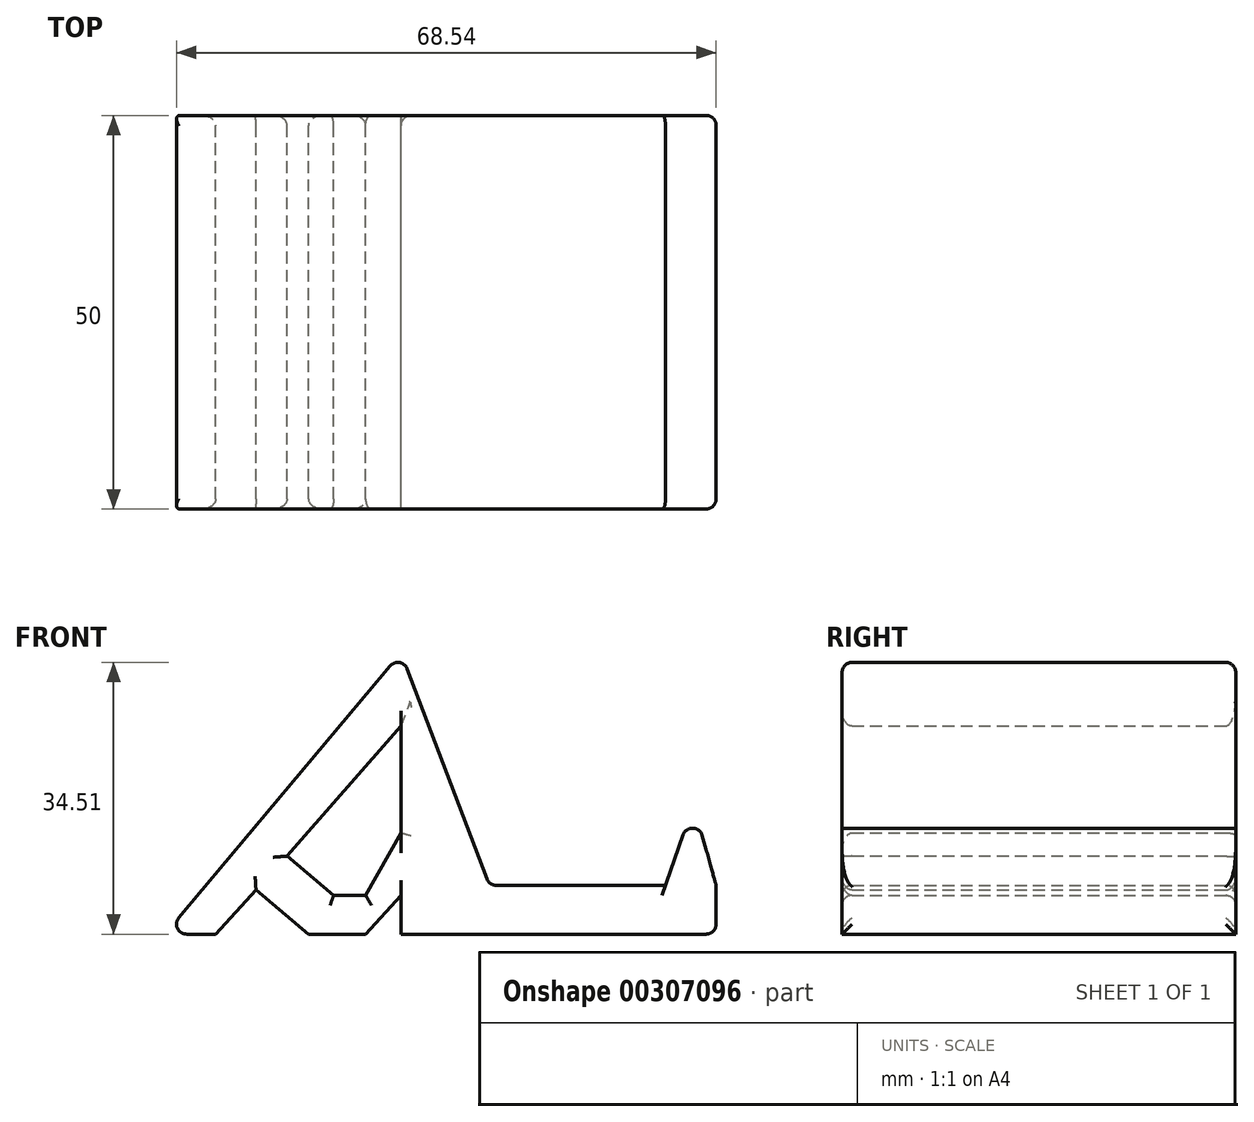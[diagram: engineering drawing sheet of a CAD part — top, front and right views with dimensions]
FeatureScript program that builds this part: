
annotation { "Feature Type Name" : "Feature", "Feature Type Description" : "" }
export const myFeature = defineFeature(function(context is Context, id is Id, definition is map)
    precondition{}
    {
        {
            var Q0;
            Q0=qCreatedBy(makeId("Front.planeOp"),FACE);
            var sketch = newSketch(context, id + "F0", { "sketchPlane" : qUnion([Q0])});
            skLineSegment(sketch, "E0", {"start": v(0, 0) * mm, "end": v(40, 0) * mm});
            skLineSegment(sketch, "E1", {"start": v(40, 0) * mm, "end": v(40, 6.2) * mm});
            skLineSegment(sketch, "E2", {"start": v(40, 6.2) * mm, "end": v(37.15, 16.43) * mm});
            skLineSegment(sketch, "E3", {"start": v(37.15, 16.43) * mm, "end": v(33.58, 6.2) * mm});
            skLineSegment(sketch, "E4", {"start": v(33.58, 6.2) * mm, "end": v(11.2, 6.2) * mm});
            skLineSegment(sketch, "E5", {"start": v(11.2, 6.2) * mm, "end": v(0, 35.72) * mm});
            skLineSegment(sketch, "E6", {"start": v(0, 35.72) * mm, "end": v(-30, 0) * mm});
            skLineSegment(sketch, "E7", {"start": v(-23.57, 0) * mm, "end": v(-30, 0) * mm});
            skLineSegment(sketch, "E8", {"start": v(-11.79, 0) * mm, "end": v(-4.52, 0) * mm});
            skLineSegment(sketch, "E9", {"start": v(-4.52, 0) * mm, "end": v(0, 4.94) * mm});
            skLineSegment(sketch, "E10", {"start": v(0, 12.86) * mm, "end": v(-4.52, 4.94) * mm});
            skLineSegment(sketch, "E11", {"start": v(-4.52, 4.94) * mm, "end": v(-8.57, 4.94) * mm});
            skLineSegment(sketch, "E12", {"start": v(-8.57, 4.94) * mm, "end": v(-14.5, 9.9) * mm});
            skLineSegment(sketch, "E13", {"start": v(-11.79, 0) * mm, "end": v(-18.45, 5.6) * mm});
            skLineSegment(sketch, "E14", {"start": v(0, 0) * mm, "end": v(0, 4.94) * mm});
            skLineSegment(sketch, "E15", {"start": v(0, 12.86) * mm, "end": v(0, 26.43) * mm});
            skLineSegment(sketch, "E16", {"start": v(0, 26.43) * mm, "end": v(-14.5, 9.9) * mm});
            skLineSegment(sketch, "E17", {"start": v(-18.45, 5.6) * mm, "end": v(-23.57, 0) * mm});
            skSolve(sketch);
        }
        {
            var Q0;
            Q0=makeQuery(id+"F0.imprint","IMPRINT",FACE,{"disambiguationData":[TD([[makeQuery(id+"F0.imprint","IMPRINT",EDGE,{"derivedFrom":sQuery(id+"F0.wireOp",EDGE,"E0")}),1.0]])]});
            extrude(context, id + "F1", {"entities" : qUnion([Q0]), "depth" : 50 * mm});
        }
        {
            var Q0;
            Q0=makeQuery(id+"F1.opExtrude","SWEPT_EDGE",EDGE,{"disambiguationData":[OSD([sQuery(id+"F0.wireOp",EDGE,"E2"),sQuery(id+"F0.wireOp",EDGE,"E3")])]});
            var Q1;
            Q1=makeQuery(id+"F1.opExtrude","CAP_EDGE",EDGE,{"disambiguationData":[OSD([sQuery(id+"F0.wireOp",EDGE,"E4")])],"isStart":false});
            var Q2;
            Q2=makeQuery(id+"F1.opExtrude","CAP_EDGE",EDGE,{"disambiguationData":[OSD([sQuery(id+"F0.wireOp",EDGE,"E1")])],"isStart":false});
            var Q3;
            Q3=makeQuery(id+"F1.opExtrude","SWEPT_FACE",FACE,{"disambiguationData":[OSD([sQuery(id+"F0.wireOp",EDGE,"E1")])]});
            var Q4;
            Q4=makeQuery(id+"F1.opExtrude","CAP_EDGE",EDGE,{"disambiguationData":[OSD([sQuery(id+"F0.wireOp",EDGE,"E5")])],"isStart":false});
            var Q5;
            Q5=makeQuery(id+"F1.opExtrude","CAP_EDGE",EDGE,{"disambiguationData":[OSD([sQuery(id+"F0.wireOp",EDGE,"E6")])],"isStart":false});
            var Q6;
            Q6=makeQuery(id+"F1.opExtrude","CAP_EDGE",EDGE,{"disambiguationData":[OSD([sQuery(id+"F0.wireOp",EDGE,"E4")])],"isStart":true});
            var Q7;
            Q7=makeQuery(id+"F1.opExtrude","CAP_EDGE",EDGE,{"disambiguationData":[OSD([sQuery(id+"F0.wireOp",EDGE,"E5")])],"isStart":true});
            var Q8;
            Q8=makeQuery(id+"F1.opExtrude","CAP_EDGE",EDGE,{"disambiguationData":[OSD([sQuery(id+"F0.wireOp",EDGE,"E6")])],"isStart":true});
            var Q9;
            Q9=makeQuery(id+"F1.opExtrude","CAP_EDGE",EDGE,{"disambiguationData":[OSD([sQuery(id+"F0.wireOp",EDGE,"E16")])],"isStart":true});
            var Q10;
            Q10=makeQuery(id+"F1.opExtrude","CAP_EDGE",EDGE,{"disambiguationData":[OSD([sQuery(id+"F0.wireOp",EDGE,"E12")])],"isStart":true});
            var Q11;
            Q11=makeQuery(id+"F1.opExtrude","CAP_EDGE",EDGE,{"disambiguationData":[OSD([sQuery(id+"F0.wireOp",EDGE,"E11")])],"isStart":true});
            var Q12;
            Q12=makeQuery(id+"F1.opExtrude","CAP_EDGE",EDGE,{"disambiguationData":[OSD([sQuery(id+"F0.wireOp",EDGE,"E10")])],"isStart":true});
            var Q13;
            Q13=makeQuery(id+"F1.opExtrude","CAP_EDGE",EDGE,{"disambiguationData":[OSD([sQuery(id+"F0.wireOp",EDGE,"E9")])],"isStart":true});
            var Q14;
            Q14=makeQuery(id+"F1.opExtrude","CAP_EDGE",EDGE,{"disambiguationData":[OSD([sQuery(id+"F0.wireOp",EDGE,"E13")])],"isStart":true});
            var Q15;
            Q15=makeQuery(id+"F1.opExtrude","CAP_EDGE",EDGE,{"disambiguationData":[OSD([sQuery(id+"F0.wireOp",EDGE,"E17")])],"isStart":true});
            var Q16;
            Q16=makeQuery(id+"F1.opExtrude","SWEPT_FACE",FACE,{"disambiguationData":[OSD([sQuery(id+"F0.wireOp",EDGE,"E6")])]});
            var Q17;
            Q17=makeQuery(id+"F1.opExtrude","SWEPT_EDGE",EDGE,{"disambiguationData":[OSD([sQuery(id+"F0.wireOp",EDGE,"E4"),sQuery(id+"F0.wireOp",EDGE,"E5")])]});
            fillet(context, id + "F2", {"entities" : qUnion([Q0, Q1, Q2, Q3, Q4, Q5, Q6, Q7, Q8, Q9, Q10, Q11, Q12, Q13, Q14, Q15, Q16, Q17]), "radius" : 1.27 * mm, "tangentPropagation" : true, "allowEdgeOverflow" : false});
        }
        {
            var Q0;
            Q0=makeQuery(id+"F1.opExtrude","CAP_EDGE",EDGE,{"disambiguationData":[OSD([sQuery(id+"F0.wireOp",EDGE,"E12")])],"isStart":false});
            var Q1;
            Q1=makeQuery(id+"F1.opExtrude","CAP_EDGE",EDGE,{"disambiguationData":[OSD([sQuery(id+"F0.wireOp",EDGE,"E16")])],"isStart":false});
            var Q2;
            Q2=makeQuery(id+"F1.opExtrude","CAP_EDGE",EDGE,{"disambiguationData":[OSD([sQuery(id+"F0.wireOp",EDGE,"E11")])],"isStart":false});
            var Q3;
            Q3=makeQuery(id+"F1.opExtrude","CAP_EDGE",EDGE,{"disambiguationData":[OSD([sQuery(id+"F0.wireOp",EDGE,"E10")])],"isStart":false});
            var Q4;
            Q4=makeQuery(id+"F1.opExtrude","CAP_EDGE",EDGE,{"disambiguationData":[OSD([sQuery(id+"F0.wireOp",EDGE,"E13")])],"isStart":false});
            var Q5;
            Q5=makeQuery(id+"F1.opExtrude","CAP_EDGE",EDGE,{"disambiguationData":[OSD([sQuery(id+"F0.wireOp",EDGE,"E17")])],"isStart":false});
            var Q6;
            Q6=makeQuery(id+"F1.opExtrude","CAP_EDGE",EDGE,{"disambiguationData":[OSD([sQuery(id+"F0.wireOp",EDGE,"E9")])],"isStart":false});
            var Q7;
            Q7=makeQuery(id+"F1.opExtrude","CAP_EDGE",EDGE,{"disambiguationData":[OSD([sQuery(id+"F0.wireOp",EDGE,"E15")])],"isStart":true});
            fillet(context, id + "F3", {"entities" : qUnion([Q0, Q1, Q2, Q3, Q4, Q5, Q6, Q7]), "radius" : 1.27 * mm, "tangentPropagation" : true, "allowEdgeOverflow" : false});
        }
    });
